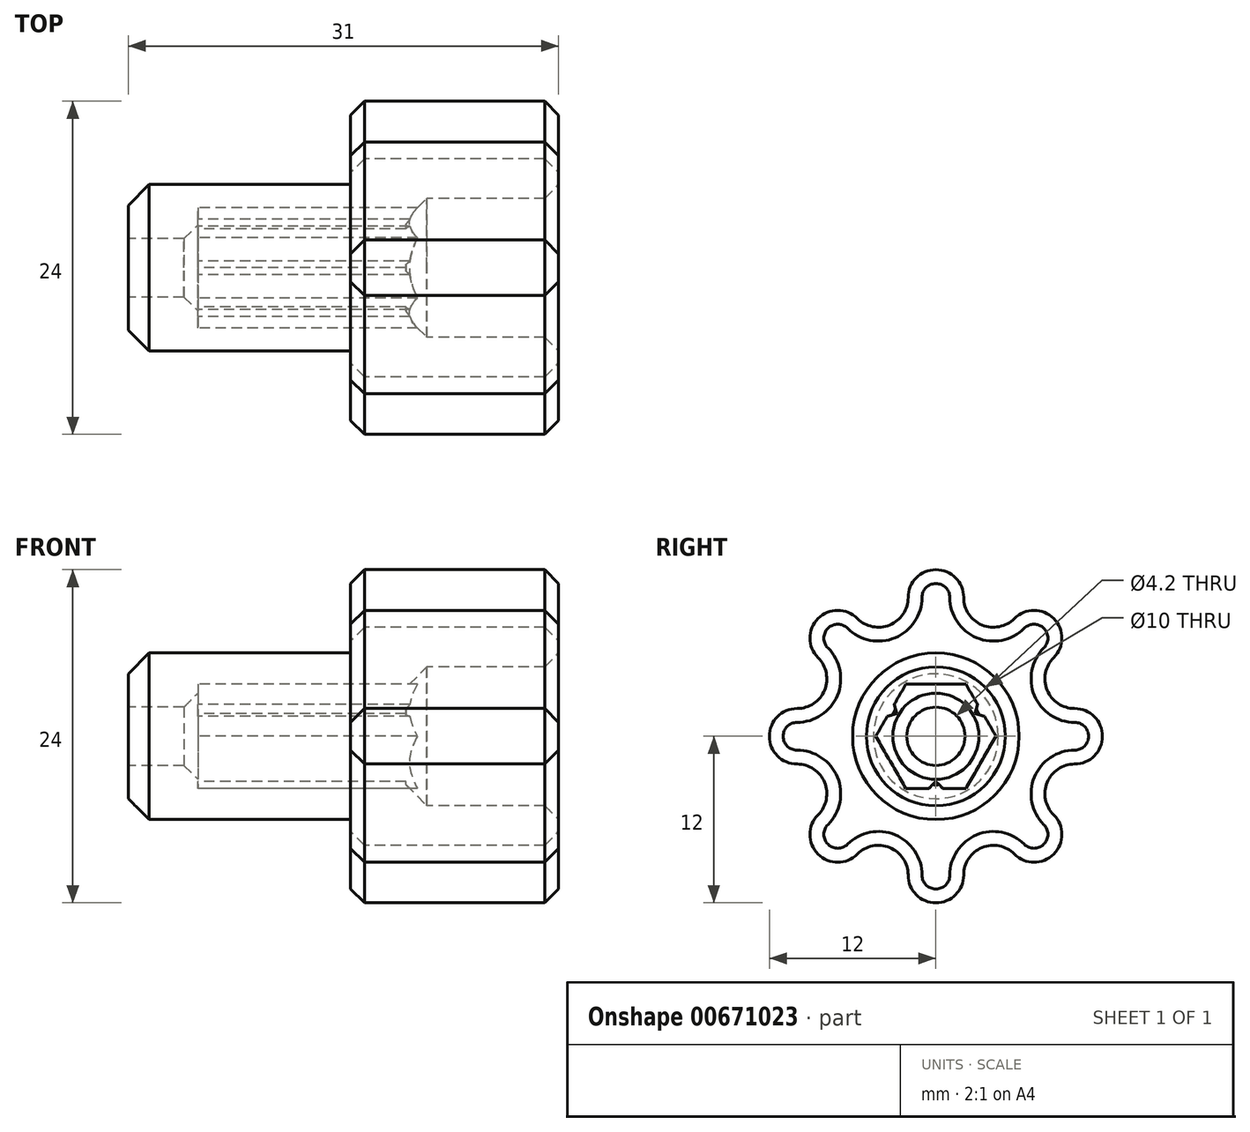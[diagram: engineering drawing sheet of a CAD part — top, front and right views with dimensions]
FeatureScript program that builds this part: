
annotation { "Feature Type Name" : "Feature", "Feature Type Description" : "" }
export const myFeature = defineFeature(function(context is Context, id is Id, definition is map)
    precondition{}
    {
        {
            var Q0;
            Q0=qCreatedBy(makeId("Right.planeOp"),FACE);
            var sketch = newSketch(context, id + "F0", { "sketchPlane" : qUnion([Q0])});
            skCircle(sketch, "E0", {"center": v(0, 0) * mm, "radius": 6 * mm});
            skCircle(sketch, "E1", {"center": v(0, 0) * mm, "radius": 2.1 * mm});
            skArc(sketch, "E2", {"start": v(2, 10) * mm, "mid": v(0, 12) * mm, "end": v(-2, 10) * mm});
            skArc(sketch, "E3", {"start": v(2, 10) * mm, "mid": v(3.32, 8.02) * mm, "end": v(5.66, 8.49) * mm});
            skArc(sketch, "E4.1.0", {"start": v(-5.66, 8.49) * mm, "mid": v(-3.32, 8.02) * mm, "end": v(-2, 10) * mm});
            skArc(sketch, "E4.1.1", {"start": v(-5.66, 8.49) * mm, "mid": v(-8.49, 8.49) * mm, "end": v(-8.49, 5.66) * mm});
            skArc(sketch, "E4.2.0", {"start": v(-10, 2) * mm, "mid": v(-8.02, 3.32) * mm, "end": v(-8.49, 5.66) * mm});
            skArc(sketch, "E4.2.1", {"start": v(-10, 2) * mm, "mid": v(-12, 0) * mm, "end": v(-10, -2) * mm});
            skArc(sketch, "E4.3.0", {"start": v(-8.49, -5.66) * mm, "mid": v(-8.02, -3.32) * mm, "end": v(-10, -2) * mm});
            skArc(sketch, "E4.3.1", {"start": v(-8.49, -5.66) * mm, "mid": v(-8.49, -8.49) * mm, "end": v(-5.66, -8.49) * mm});
            skArc(sketch, "E4.4.0", {"start": v(-2, -10) * mm, "mid": v(-3.32, -8.02) * mm, "end": v(-5.66, -8.49) * mm});
            skArc(sketch, "E4.4.1", {"start": v(-2, -10) * mm, "mid": v(0, -12) * mm, "end": v(2, -10) * mm});
            skArc(sketch, "E4.5.0", {"start": v(5.66, -8.49) * mm, "mid": v(3.32, -8.02) * mm, "end": v(2, -10) * mm});
            skArc(sketch, "E4.5.1", {"start": v(5.66, -8.49) * mm, "mid": v(8.49, -8.49) * mm, "end": v(8.49, -5.66) * mm});
            skArc(sketch, "E4.6.0", {"start": v(10, -2) * mm, "mid": v(8.02, -3.32) * mm, "end": v(8.49, -5.66) * mm});
            skArc(sketch, "E4.6.1", {"start": v(10, -2) * mm, "mid": v(12, 0) * mm, "end": v(10, 2) * mm});
            skArc(sketch, "E4.7.0", {"start": v(8.49, 5.66) * mm, "mid": v(8.02, 3.32) * mm, "end": v(10, 2) * mm});
            skArc(sketch, "E4.7.1", {"start": v(8.49, 5.66) * mm, "mid": v(8.49, 8.49) * mm, "end": v(5.66, 8.49) * mm});
            skSolve(sketch);
        }
        {
            var Q0;
            Q0=qSketchRegion(id+"F0",true);
            var Q1;
            Q1=makeQuery(id+"F0.imprint","IMPRINT",FACE,{"disambiguationData":[TD([[makeQuery(id+"F0.imprint","IMPRINT",EDGE,{"derivedFrom":sQuery(id+"F0.wireOp",EDGE,"E0")}),1.0]])]});
            extrude(context, id + "F1", {"entities" : qUnion([Q0, Q1]), "depth" : 15 * mm, "offsetDistance" : 25 * mm});
        }
        {
            var Q0;
            Q0=makeQuery(id+"F0.imprint","IMPRINT",FACE,{"disambiguationData":[TD([[makeQuery(id+"F0.imprint","IMPRINT",EDGE,{"derivedFrom":sQuery(id+"F0.wireOp",EDGE,"E0")}),1.0]])]});
            extrude(context, id + "F2", {"entities" : qUnion([Q0]), "operationType" : NewBodyOperationType.ADD, "oppositeDirection" : true, "depth" : 16 * mm, "offsetDistance" : 25 * mm});
        }
        {
            var Q0;
            Q0=makeQuery(id+"F2.opExtrude","CAP_FACE",FACE,{"disambiguationData":[OSD([sQuery(id+"F0.wireOp",EDGE,"E0"),sQuery(id+"F0.wireOp",EDGE,"E1")])],"isStart":false});
            cPlane(context, id + "F3", {"entities" : qUnion([Q0]), "cplaneType" : CPlaneType.OFFSET, "offset" : 5 * mm, "oppositeDirection" : true, "width" : 150 * mm, "height" : 150 * mm});
        }
        {
            var Q0;
            Q0=qCreatedBy(id+"F3.planeOp",FACE);
            var sketch = newSketch(context, id + "F4", { "sketchPlane" : qUnion([Q0])});
            skCircle(sketch, "E5.cCircle", {"center": v(0, 0) * mm, "radius": 3.75 * mm, "construction": true});
            skLineSegment(sketch, "E5.0", {"start": v(4.33, 0) * mm, "end": v(2.17, -3.75) * mm});
            skLineSegment(sketch, "E5.1", {"start": v(2.17, -3.75) * mm, "end": v(0.5, -3.75) * mm});
            skLineSegment(sketch, "E5.2", {"start": v(-2.17, -3.75) * mm, "end": v(-4.33, 0) * mm});
            skLineSegment(sketch, "E5.4", {"start": v(-2.17, 3.75) * mm, "end": v(2.17, 3.75) * mm});
            skPoint(sketch, "E5.0.midPoint", {"position": v(3.25, -1.87) * mm});
            skLineSegment(sketch, "E6", {"start": v(-0.5, -3.75) * mm, "end": v(0, -3.25) * mm});
            skLineSegment(sketch, "E7", {"start": v(0, -3.25) * mm, "end": v(0.5, -3.75) * mm});
            skLineSegment(sketch, "E8.trimOffspring", {"start": v(-0.5, -3.75) * mm, "end": v(-2.17, -3.75) * mm});
            skLineSegment(sketch, "E9.1.0", {"start": v(3.5, 1.44) * mm, "end": v(4.33, 0) * mm});
            skLineSegment(sketch, "E9.1.1", {"start": v(3.5, 1.44) * mm, "end": v(2.81, 1.62) * mm});
            skLineSegment(sketch, "E9.1.2", {"start": v(2.81, 1.62) * mm, "end": v(3, 2.3) * mm});
            skLineSegment(sketch, "E9.1.3", {"start": v(2.17, 3.75) * mm, "end": v(3, 2.3) * mm});
            skLineSegment(sketch, "E9.2.0", {"start": v(-3, 2.3) * mm, "end": v(-2.17, 3.75) * mm});
            skLineSegment(sketch, "E9.2.1", {"start": v(-3, 2.3) * mm, "end": v(-2.81, 1.62) * mm});
            skLineSegment(sketch, "E9.2.2", {"start": v(-2.81, 1.62) * mm, "end": v(-3.5, 1.44) * mm});
            skLineSegment(sketch, "E9.2.3", {"start": v(-4.33, 0) * mm, "end": v(-3.5, 1.44) * mm});
            skSolve(sketch);
        }
        {
            var Q0;
            Q0 = qSketchRegion(id + "F4", true);
            extrude(context, id + "F5", {"entities" : qUnion([Q0]), "operationType" : NewBodyOperationType.REMOVE, "endBound" : BoundingType.THROUGH_ALL, "oppositeDirection" : true, "depth" : 25 * mm, "offsetDistance" : 25 * mm});
        }
        {
            var Q0;
            Q0=qCreatedBy(id+"F3.planeOp",FACE);
            cPlane(context, id + "F6", {"entities" : qUnion([Q0]), "cplaneType" : CPlaneType.OFFSET, "offset" : 15 * mm, "oppositeDirection" : true, "width" : 150 * mm, "height" : 150 * mm});
        }
        {
            var Q0;
            Q0=qCreatedBy(id+"F6.planeOp",FACE);
            var sketch = newSketch(context, id + "F7", { "sketchPlane" : qUnion([Q0])});
            skCircle(sketch, "E10", {"center": v(0, 0) * mm, "radius": 5 * mm});
            skSolve(sketch);
        }
        {
            var Q0;
            Q0 = qSketchRegion(id + "F7", true);
            extrude(context, id + "F8", {"entities" : qUnion([Q0]), "operationType" : NewBodyOperationType.REMOVE, "endBound" : BoundingType.THROUGH_ALL, "oppositeDirection" : true, "depth" : 25 * mm, "offsetDistance" : 25 * mm});
        }
        {
            var Q0;
            Q0=makeQuery(id+"F1.opExtrude","CAP_FACE",FACE,{"disambiguationData":[OSD([sQuery(id+"F0.wireOp",EDGE,"E1"),sQuery(id+"F0.wireOp",EDGE,"E2"),sQuery(id+"F0.wireOp",EDGE,"E3"),sQuery(id+"F0.wireOp",EDGE,"E4.1.0"),sQuery(id+"F0.wireOp",EDGE,"E4.1.1"),sQuery(id+"F0.wireOp",EDGE,"E4.2.0"),sQuery(id+"F0.wireOp",EDGE,"E4.2.1"),sQuery(id+"F0.wireOp",EDGE,"E4.3.0"),sQuery(id+"F0.wireOp",EDGE,"E4.3.1"),sQuery(id+"F0.wireOp",EDGE,"E4.4.0"),sQuery(id+"F0.wireOp",EDGE,"E4.4.1"),sQuery(id+"F0.wireOp",EDGE,"E4.5.0"),sQuery(id+"F0.wireOp",EDGE,"E4.5.1"),sQuery(id+"F0.wireOp",EDGE,"E4.6.0"),sQuery(id+"F0.wireOp",EDGE,"E4.6.1"),sQuery(id+"F0.wireOp",EDGE,"E4.7.0"),sQuery(id+"F0.wireOp",EDGE,"E4.7.1")])],"isStart":false});
            var Q1;
            Q1=makeQuery(id+"F1.opExtrude","CAP_EDGE",EDGE,{"disambiguationData":[OSD([sQuery(id+"F0.wireOp",EDGE,"E2")])],"isStart":true});
            var Q2;
            {var subQ0=sQuery(id+"F0.wireOp",EDGE,"E1");Q2=makeQuery(id+"F5.boolean.opBoolean","INTERSECT",EDGE,{"derivedFrom":[makeQuery(id+"F2.boolean.opBoolean","MERGE",FACE,{"derivedFrom":[makeQuery(id+"F1.opExtrude","SWEPT_FACE",FACE,{"disambiguationData":[OSD([subQ0])]}),makeQuery(id+"F2.opExtrude","SWEPT_FACE",FACE,{"disambiguationData":[OSD([subQ0])]})]}),makeQuery(id+"F5.opExtrude","CAP_FACE",FACE,{"disambiguationData":[OSD([sQuery(id+"F4.wireOp",EDGE,"E5.0"),sQuery(id+"F4.wireOp",EDGE,"E5.1"),sQuery(id+"F4.wireOp",EDGE,"E5.2"),sQuery(id+"F4.wireOp",EDGE,"E5.4"),sQuery(id+"F4.wireOp",EDGE,"E6"),sQuery(id+"F4.wireOp",EDGE,"E7"),sQuery(id+"F4.wireOp",EDGE,"E8.trimOffspring"),sQuery(id+"F4.wireOp",EDGE,"E9.1.0"),sQuery(id+"F4.wireOp",EDGE,"E9.1.1"),sQuery(id+"F4.wireOp",EDGE,"E9.1.2"),sQuery(id+"F4.wireOp",EDGE,"E9.1.3"),sQuery(id+"F4.wireOp",EDGE,"E9.2.0"),sQuery(id+"F4.wireOp",EDGE,"E9.2.1"),sQuery(id+"F4.wireOp",EDGE,"E9.2.2"),sQuery(id+"F4.wireOp",EDGE,"E9.2.3")])],"isStart":true})]});}
            chamfer(context, id + "F9", {"entities" : qUnion([Q0, Q1, Q2]), "width" : 1 * mm, "tangentPropagation" : true});
        }
        {
            var Q0;
            Q0=makeQuery(id+"F2.opExtrude","CAP_EDGE",EDGE,{"disambiguationData":[OSD([sQuery(id+"F0.wireOp",EDGE,"E0")])],"isStart":false});
            var Q1;
            Q1=makeQuery(id+"F2.opExtrude","CAP_EDGE",EDGE,{"disambiguationData":[OSD([sQuery(id+"F0.wireOp",EDGE,"E0")])],"isStart":true});
            var Q2;
            Q2=makeQuery(id+"F8.boolean.opBoolean","COPY",EDGE,{"derivedFrom":makeQuery(id+"F8.opExtrude","CAP_EDGE",EDGE,{"disambiguationData":[OSD([sQuery(id+"F7.wireOp",EDGE,"E10")])],"isStart":true})});
            chamfer(context, id + "F10", {"entities" : qUnion([Q0, Q1, Q2]), "width" : 1.5 * mm, "tangentPropagation" : true});
        }
    });
